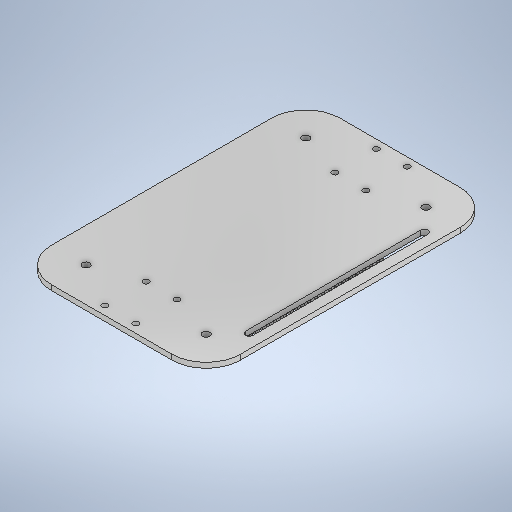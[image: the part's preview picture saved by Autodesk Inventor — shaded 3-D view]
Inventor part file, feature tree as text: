
AUTODESK INVENTOR PART (.ipt)
format: ipt  version: 2025.2 (Build 292293000, 293)  size: 378,880 bytes
history: native  units: mm
features: sketch x4, extrude x3, plane x3, hole x2, fillet x1, pattern_linear x1
ambient origin geometry x8: Origin, YZ Plane, XZ Plane, XY Plane, X Axis, Y Axis, Z Axis, Center Point
bodies: Solid1 (feature_tree)
feature tree (14):
  sketch  "Sketch1"  dims[d4=110.0mm d5=168.0mm]
  extrude  "Extrusion2"  Depth=168.0mm
  hole  "Hole1"  [1 undecoded]
  fillet  "Fillet1"  Radius=18.0mm
  plane  "Work Plane1"
  plane  "Work Plane2"
  hole  "Hole2"  [1 undecoded]
  extrude  "Extrusion3"  Depth=24.0mm
  plane  "Work Plane3"
  extrude  "Extrusion4"  Depth=20.0mm
  pattern_linear  "Rectangular Pattern1"  Spacing1=-84.0mm  [1 undecoded]
  sketch  "Sketch2"  dims[d20=3.0mm d21=0.0mm d22=5.0mm d23=18.0mm]
  sketch  "Sketch4"  dims[d24=24.0mm d25=5.0mm]
  sketch  "Sketch5"  dims[d26=18.0mm d27=24.0mm d28=3.4mm d29=6.0mm d30=4.0mm d31=2.0mm d32=90.0deg d33=8.0mm d34=20.594885mm d35=20.0mm d36=-84.0mm d37=-55.0mm d38=4.3mm d39=6.0mm d40=4.0mm d41=2.0mm d42=90.0deg d43=8.0mm d44=20.594885mm d45=8.0mm d46=102.0mm d47=8.0mm d48=4.3mm d49=0.0mm d50=0.0mm d51=5.0mm d52=2.0mm d53=85.0mm d54=5.0mm d55=17.0mm d56=0.0mm d57=230.0mm d59=4.0mm]
note: 3 required parameter values undecoded (feature->parameter linkage not recoverable at this tier; creation-order binding heuristic only, values carry confidence <= 0.55)
